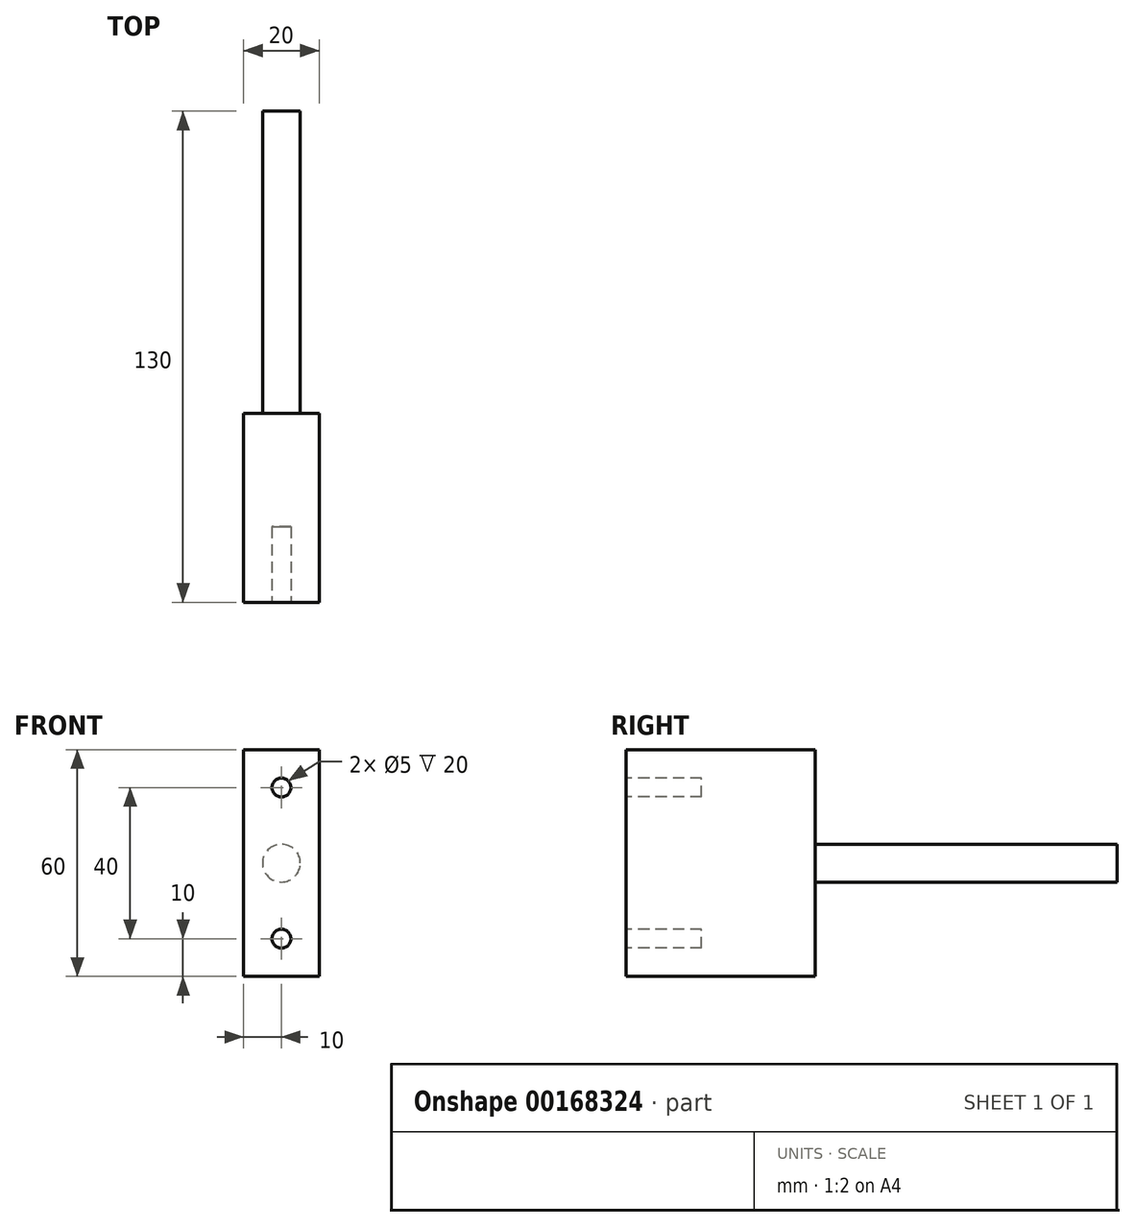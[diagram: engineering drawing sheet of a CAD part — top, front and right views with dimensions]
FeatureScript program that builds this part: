
annotation { "Feature Type Name" : "Feature", "Feature Type Description" : "" }
export const myFeature = defineFeature(function(context is Context, id is Id, definition is map)
    precondition{}
    {
        {
            var Q0;
            Q0=qCreatedBy(makeId("Top.planeOp"),FACE);
            var sketch = newSketch(context, id + "F0", { "sketchPlane" : qUnion([Q0])});
            skLineSegment(sketch, "E0.bottom", {"start": v(-10, 25) * mm, "end": v(10, 25) * mm});
            skLineSegment(sketch, "E0.top", {"start": v(-10, -25) * mm, "end": v(10, -25) * mm});
            skLineSegment(sketch, "E0.left", {"start": v(-10, 25) * mm, "end": v(-10, -25) * mm});
            skLineSegment(sketch, "E0.right", {"start": v(10, 25) * mm, "end": v(10, -25) * mm});
            skPoint(sketch, "E0.middle", {"position": v(0, 0) * mm});
            skSolve(sketch);
        }
        {
            var Q0;
            Q0=makeQuery(id+"F0.imprint","IMPRINT",FACE,{"disambiguationData":[TD([[makeQuery(id+"F0.imprint","IMPRINT",EDGE,{"derivedFrom":sQuery(id+"F0.wireOp",EDGE,"E0.bottom")}),-1.0]])]});
            extrude(context, id + "F1", {"entities" : qUnion([Q0]), "depth" : 60 * mm});
        }
        {
            var Q0;
            Q0=makeQuery(id+"F1.opExtrude","SWEPT_FACE",FACE,{"disambiguationData":[OSD([sQuery(id+"F0.wireOp",EDGE,"E0.top")])]});
            var sketch = newSketch(context, id + "F2", { "sketchPlane" : qUnion([Q0])});
            skCircle(sketch, "E1", {"center": v(0, 10) * mm, "radius": 2.5 * mm});
            skCircle(sketch, "E2", {"center": v(0, 50) * mm, "radius": 2.5 * mm});
            skPoint(sketch, "E2.centerSnap0", {"position": v(0, 60) * mm});
            skSolve(sketch);
        }
        {
            var Q0;
            Q0=makeQuery(id+"F2.imprint","IMPRINT",FACE,{"disambiguationData":[TD([[makeQuery(id+"F2.imprint","IMPRINT",EDGE,{"derivedFrom":sQuery(id+"F2.wireOp",EDGE,"E2")}),1.0]])]});
            var Q1;
            Q1=makeQuery(id+"F2.imprint","IMPRINT",FACE,{"disambiguationData":[TD([[makeQuery(id+"F2.imprint","IMPRINT",EDGE,{"derivedFrom":sQuery(id+"F2.wireOp",EDGE,"E1")}),1.0]])]});
            extrude(context, id + "F3", {"entities" : qUnion([Q0, Q1]), "operationType" : NewBodyOperationType.REMOVE, "oppositeDirection" : true, "depth" : 20 * mm});
        }
        {
            var Q0;
            Q0=makeQuery(id+"F1.opExtrude","SWEPT_FACE",FACE,{"disambiguationData":[OSD([sQuery(id+"F0.wireOp",EDGE,"E0.bottom")])]});
            var sketch = newSketch(context, id + "F4", { "sketchPlane" : qUnion([Q0])});
            skCircle(sketch, "E3", {"center": v(0, 30) * mm, "radius": 5 * mm});
            skPoint(sketch, "E3.centerSnap0", {"position": v(-10, 30) * mm});
            skSolve(sketch);
        }
        {
            var Q0;
            Q0=makeQuery(id+"F4.imprint","IMPRINT",FACE,{"disambiguationData":[TD([[makeQuery(id+"F4.imprint","IMPRINT",EDGE,{"derivedFrom":sQuery(id+"F4.wireOp",EDGE,"E3")}),1.0]])]});
            extrude(context, id + "F5", {"entities" : qUnion([Q0]), "operationType" : NewBodyOperationType.ADD, "depth" : 80 * mm});
        }
    });
